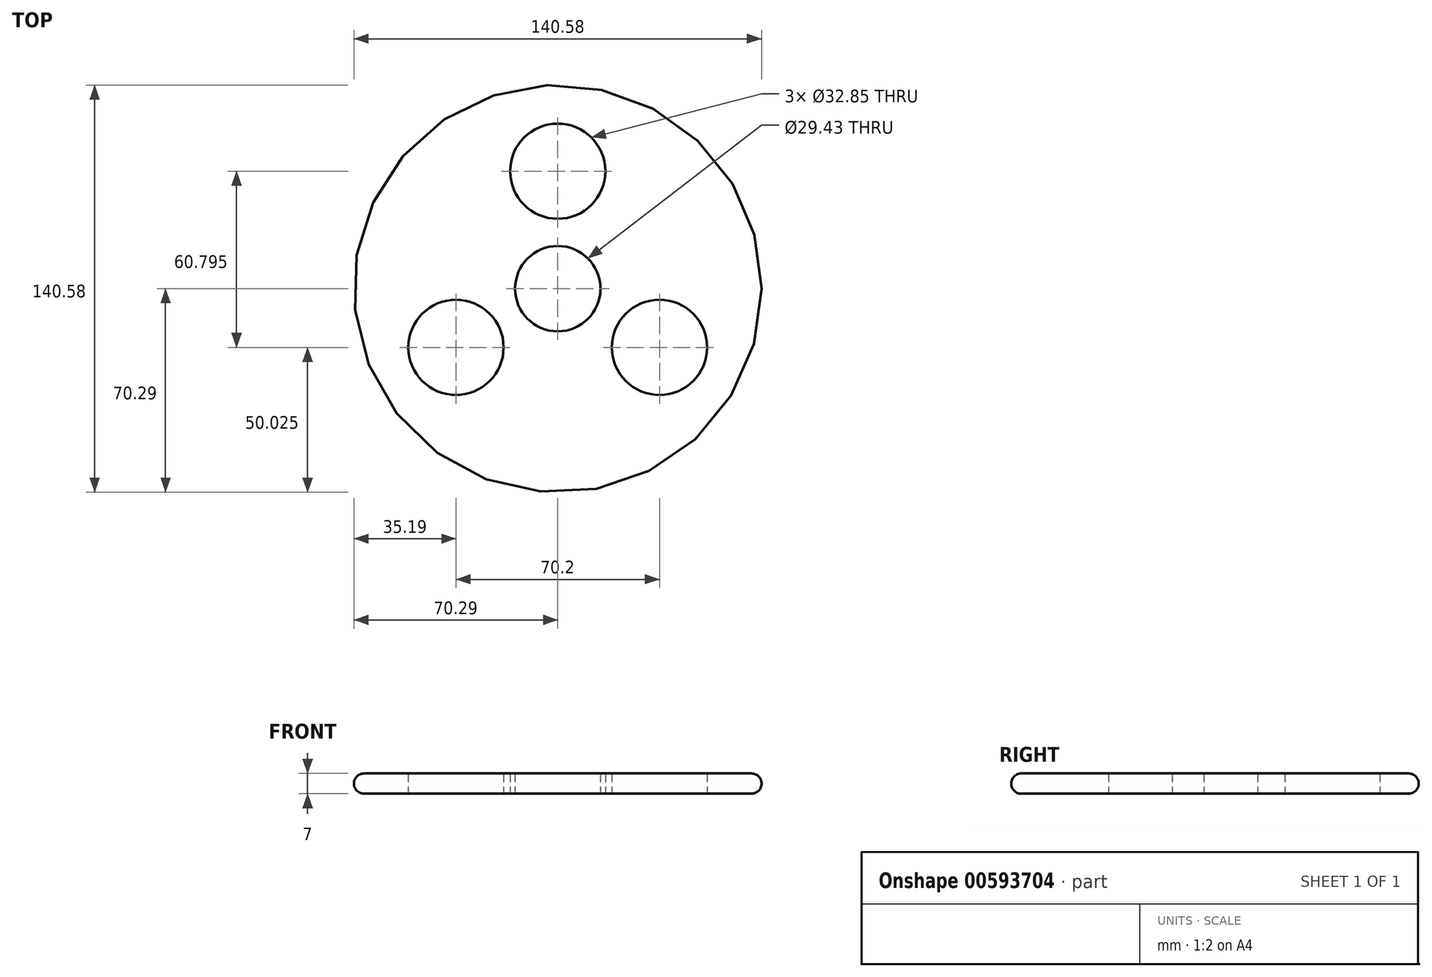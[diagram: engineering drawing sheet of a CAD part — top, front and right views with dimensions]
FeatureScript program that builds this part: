
annotation { "Feature Type Name" : "Feature", "Feature Type Description" : "" }
export const myFeature = defineFeature(function(context is Context, id is Id, definition is map)
    precondition{}
    {
        {
            var Q0;
            Q0=qCreatedBy(makeId("Top.planeOp"),FACE);
            var sketch = newSketch(context, id + "F0", { "sketchPlane" : qUnion([Q0])});
            skCircle(sketch, "E0", {"center": v(0, 0) * mm, "radius": 14.72 * mm});
            skPoint(sketch, "E1.center.orphan", {"position": v(0, 40.53) * mm});
            skCircle(sketch, "E2", {"center": v(0, 40.53) * mm, "radius": 16.43 * mm});
            skCircle(sketch, "E3.1.0", {"center": v(-35.1, -20.26) * mm, "radius": 16.43 * mm});
            skCircle(sketch, "E3.2.0", {"center": v(35.1, -20.26) * mm, "radius": 16.43 * mm});
            skCircle(sketch, "E4", {"center": v(0, 0) * mm, "radius": 70.29 * mm});
            skSolve(sketch);
        }
        {
            var Q0;
            Q0=makeQuery(id+"F0.imprint","IMPRINT",FACE,{"disambiguationData":[TD([[makeQuery(id+"F0.imprint","IMPRINT",EDGE,{"derivedFrom":sQuery(id+"F0.wireOp",EDGE,"E0")}),-1.0]])]});
            extrude(context, id + "F1", {"entities" : qUnion([Q0]), "depth" : 7 * mm, "offsetDistance" : 25 * mm});
        }
        {
            var Q0;
            Q0=makeQuery(id+"F1.opExtrude","CAP_EDGE",EDGE,{"disambiguationData":[OSD([sQuery(id+"F0.wireOp",EDGE,"E4")])],"isStart":false});
            var Q1;
            Q1=makeQuery(id+"F1.opExtrude","CAP_EDGE",EDGE,{"disambiguationData":[OSD([sQuery(id+"F0.wireOp",EDGE,"E4")])],"isStart":true});
            fillet(context, id + "F2", {"entities" : qUnion([Q0, Q1]), "radius" : 3.5 * mm, "tangentPropagation" : true, "allowEdgeOverflow" : false});
        }
    });
